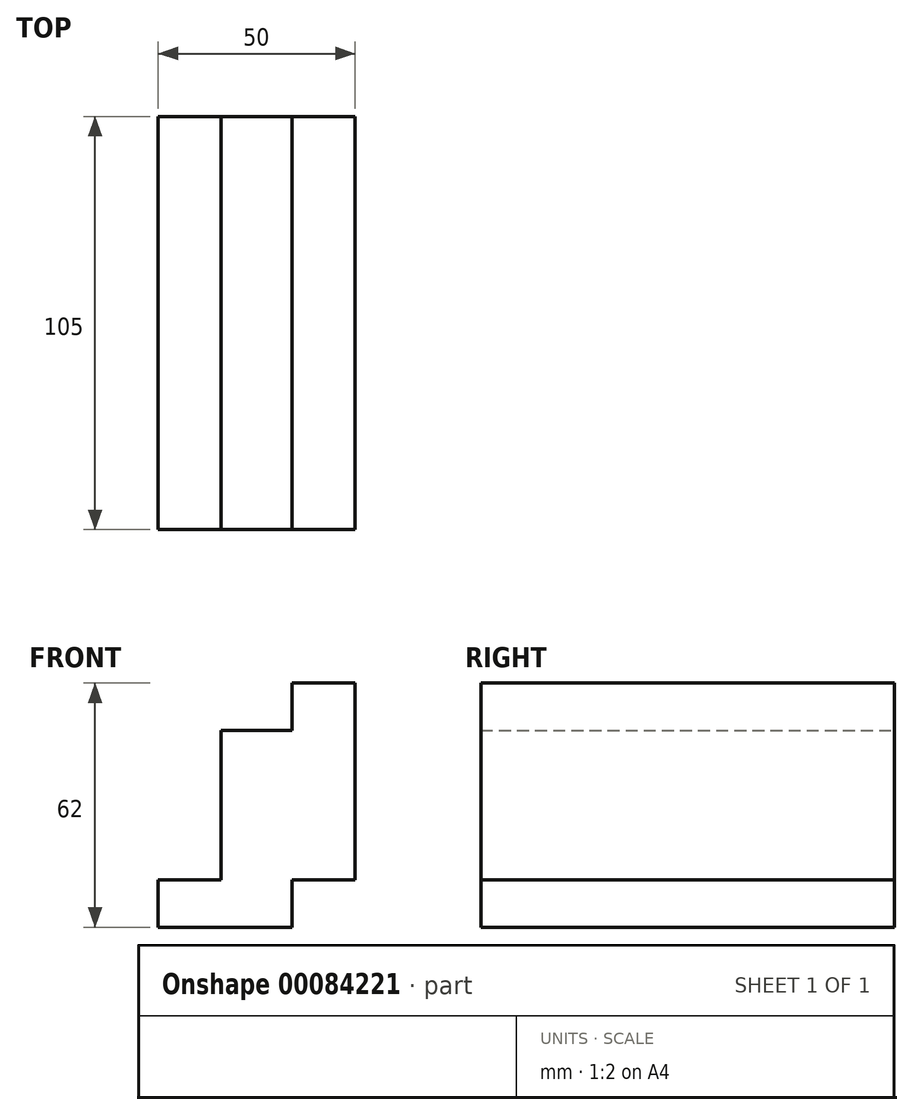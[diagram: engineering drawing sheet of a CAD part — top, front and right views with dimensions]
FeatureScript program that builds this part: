
annotation { "Feature Type Name" : "Feature", "Feature Type Description" : "" }
export const myFeature = defineFeature(function(context is Context, id is Id, definition is map)
    precondition{}
    {
        {
            var Q0;
            Q0=qCreatedBy(makeId("Front.planeOp"),FACE);
            var sketch = newSketch(context, id + "F0", { "sketchPlane" : qUnion([Q0])});
            skLineSegment(sketch, "E0.bottom", {"start": v(8.56, 25.04) * mm, "end": v(24.56, 25.04) * mm});
            skLineSegment(sketch, "E0.top", {"start": v(-25.44, -36.96) * mm, "end": v(8.56, -36.96) * mm});
            skLineSegment(sketch, "E0.left", {"start": v(-25.44, -24.96) * mm, "end": v(-25.44, -36.96) * mm});
            skLineSegment(sketch, "E0.right", {"start": v(24.56, 25.04) * mm, "end": v(24.56, -24.96) * mm});
            skLineSegment(sketch, "E1", {"start": v(8.56, 25.04) * mm, "end": v(8.56, 13.04) * mm});
            skLineSegment(sketch, "E2", {"start": v(8.56, 13.04) * mm, "end": v(-9.44, 13.04) * mm});
            skLineSegment(sketch, "E3", {"start": v(-9.44, 13.04) * mm, "end": v(-9.44, -24.96) * mm});
            skLineSegment(sketch, "E4", {"start": v(-9.44, -24.96) * mm, "end": v(-25.44, -24.96) * mm});
            skLineSegment(sketch, "E5", {"start": v(8.56, -36.96) * mm, "end": v(8.56, -24.96) * mm});
            skLineSegment(sketch, "E6", {"start": v(8.56, -24.96) * mm, "end": v(24.56, -24.96) * mm});
            skSolve(sketch);
        }
        {
            var Q0;
            Q0=makeQuery(id+"F0.imprint","IMPRINT",FACE,{"disambiguationData":[TD([[makeQuery(id+"F0.imprint","IMPRINT",EDGE,{"derivedFrom":sQuery(id+"F0.wireOp",EDGE,"E0.bottom")}),-1.0]])]});
            extrude(context, id + "F1", {"entities" : qUnion([Q0]), "depth" : 105 * mm});
        }
        {
            var Q0;
            Q0=makeQuery(id+"F1.opExtrude","SWEPT_FACE",FACE,{"disambiguationData":[OSD([sQuery(id+"F0.wireOp",EDGE,"E3")])]});
            var sketch = newSketch(context, id + "F2", { "sketchPlane" : qUnion([Q0])});
            skCircle(sketch, "E7", {"center": v(32, -6.96) * mm, "radius": 10 * mm});
            skSolve(sketch);
        }
        {
            var Q0;
            Q0=sQuery(id+"F2.wireOp",EDGE,"E7");
            extrude(context, id + "F3", {"bodyType" : ToolBodyType.SURFACE, "surfaceEntities" : qUnion([Q0]), "endBound" : BoundingType.THROUGH_ALL, "oppositeDirection" : true, "depth" : 25 * mm});
        }
    });
